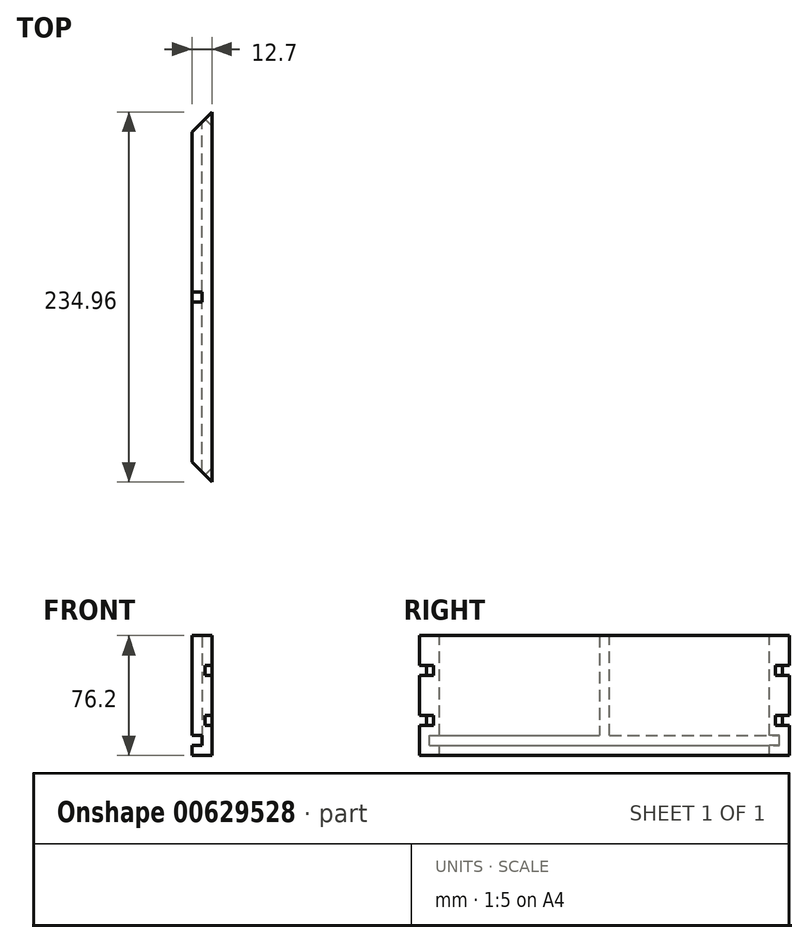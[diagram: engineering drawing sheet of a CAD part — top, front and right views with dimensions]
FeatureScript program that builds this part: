
annotation { "Feature Type Name" : "Feature", "Feature Type Description" : "" }
export const myFeature = defineFeature(function(context is Context, id is Id, definition is map)
    precondition{}
    {
        {
            var Q0;
            Q0=qCreatedBy(makeId("Right.planeOp"),FACE);
            var sketch = newSketch(context, id + "F0", { "sketchPlane" : qUnion([Q0])});
            skLineSegment(sketch, "E0.bottom", {"start": v(-117.47, 0) * mm, "end": v(117.48, 0) * mm});
            skLineSegment(sketch, "E0.top", {"start": v(-117.47, 76.2) * mm, "end": v(117.47, 76.2) * mm});
            skLineSegment(sketch, "E0.left", {"start": v(-117.47, 0) * mm, "end": v(-117.48, 76.2) * mm});
            skLineSegment(sketch, "E0.right", {"start": v(117.48, 0) * mm, "end": v(117.47, 76.2) * mm});
            skSolve(sketch);
        }
        {
            var Q0;
            Q0=makeQuery(id+"F0.imprint","IMPRINT",FACE,{"disambiguationData":[TD([[makeQuery(id+"F0.imprint","IMPRINT",EDGE,{"derivedFrom":sQuery(id+"F0.wireOp",EDGE,"E0.bottom")}),1.0]])]});
            extrude(context, id + "F1", {"entities" : qUnion([Q0]), "depth" : 12.7 * mm, "offsetDistance" : 25.4 * mm});
        }
        {
            var Q0;
            Q0=makeQuery(id+"F1.opExtrude","SWEPT_FACE",FACE,{"disambiguationData":[OSD([sQuery(id+"F0.wireOp",EDGE,"E0.right")])]});
            var sketch = newSketch(context, id + "F2", { "sketchPlane" : qUnion([Q0])});
            skLineSegment(sketch, "E1.bottom", {"start": v(0, 12.7) * mm, "end": v(-6.35, 12.7) * mm});
            skLineSegment(sketch, "E1.top", {"start": v(0, 6.35) * mm, "end": v(-6.35, 6.35) * mm});
            skLineSegment(sketch, "E1.left", {"start": v(0, 12.7) * mm, "end": v(0, 6.35) * mm});
            skLineSegment(sketch, "E1.right", {"start": v(-6.35, 12.7) * mm, "end": v(-6.35, 6.35) * mm});
            skSolve(sketch);
        }
        {
            var Q0;
            Q0 = qSketchRegion(id + "F2", true);
            extrude(context, id + "F3", {"entities" : qUnion([Q0]), "operationType" : NewBodyOperationType.REMOVE, "endBound" : BoundingType.THROUGH_ALL, "oppositeDirection" : true, "depth" : 25.4 * mm, "offsetDistance" : 25.4 * mm});
        }
        {
            var Q0;
            Q0=makeQuery(id+"F1.opExtrude","SWEPT_FACE",FACE,{"disambiguationData":[OSD([sQuery(id+"F0.wireOp",EDGE,"E0.top")])]});
            var sketch = newSketch(context, id + "F4", { "sketchPlane" : qUnion([Q0])});
            skLineSegment(sketch, "E2", {"start": v(12.7, 117.47) * mm, "end": v(0, 104.77) * mm});
            skLineSegment(sketch, "E3", {"start": v(0, 104.77) * mm, "end": v(0, 117.47) * mm});
            skLineSegment(sketch, "E4", {"start": v(0, 117.47) * mm, "end": v(12.7, 117.47) * mm});
            skLineSegment(sketch, "E5.MirrorCS", {"start": v(0, -117.47) * mm, "end": v(12.7, -117.47) * mm});
            skLineSegment(sketch, "E6.MirrorCS", {"start": v(12.7, -117.47) * mm, "end": v(0, -104.77) * mm});
            skLineSegment(sketch, "E7.MirrorCS", {"start": v(0, -104.77) * mm, "end": v(0, -117.47) * mm});
            skSolve(sketch);
        }
        {
            var Q0;
            Q0 = qSketchRegion(id + "F4", true);
            extrude(context, id + "F5", {"entities" : qUnion([Q0]), "operationType" : NewBodyOperationType.REMOVE, "endBound" : BoundingType.THROUGH_ALL, "oppositeDirection" : true, "depth" : 25.4 * mm, "offsetDistance" : 25.4 * mm});
        }
        {
            var Q0;
            {var subQ0=sQuery(id+"F0.wireOp",EDGE,"E0.top");var subQ1=sQuery(id+"F0.wireOp",EDGE,"E0.left");var subQ2=sQuery(id+"F0.wireOp",EDGE,"E0.right");Q0=makeQuery(id+"F3.boolean.opBoolean","SPLIT",FACE,{"disambiguationData":[TD([makeQuery(id+"F1.opExtrude","SWEPT_FACE",FACE,{"disambiguationData":[OSD([subQ0])]})])],"derivedFrom":makeQuery(id+"F1.opExtrude","CAP_FACE",FACE,{"disambiguationData":[OSD([sQuery(id+"F0.wireOp",EDGE,"E0.bottom"),subQ0,subQ1,subQ2])],"isStart":true})});}
            var sketch = newSketch(context, id + "F6", { "sketchPlane" : qUnion([Q0])});
            skLineSegment(sketch, "E8", {"start": v(-3.17, 12.7) * mm, "end": v(-3.18, 76.2) * mm});
            skLineSegment(sketch, "E9", {"start": v(3.17, 76.2) * mm, "end": v(3.18, 12.7) * mm});
            skLineSegment(sketch, "E10", {"start": v(-3.18, 76.2) * mm, "end": v(3.17, 76.2) * mm});
            skLineSegment(sketch, "E11", {"start": v(-3.17, 12.7) * mm, "end": v(3.18, 12.7) * mm});
            skSolve(sketch);
        }
        {
            var Q0;
            Q0 = qSketchRegion(id + "F6", true);
            extrude(context, id + "F7", {"entities" : qUnion([Q0]), "operationType" : NewBodyOperationType.REMOVE, "oppositeDirection" : true, "depth" : 6.35 * mm, "offsetDistance" : 25.4 * mm});
        }
        {
            var Q0;
            Q0=makeQuery(id+"F5.boolean.opBoolean","COPY",FACE,{"derivedFrom":makeQuery(id+"F5.opExtrude","SWEPT_FACE",FACE,{"disambiguationData":[OSD([sQuery(id+"F4.wireOp",EDGE,"E6.MirrorCS")])]})});
            var sketch = newSketch(context, id + "F8", { "sketchPlane" : qUnion([Q0])});
            skLineSegment(sketch, "E12.bottom", {"start": v(92.05, 57.15) * mm, "end": v(85.7, 57.15) * mm});
            skLineSegment(sketch, "E12.top", {"start": v(92.05, 50.8) * mm, "end": v(85.7, 50.8) * mm});
            skLineSegment(sketch, "E12.left", {"start": v(92.05, 57.15) * mm, "end": v(92.05, 50.8) * mm});
            skLineSegment(sketch, "E12.right", {"start": v(85.7, 57.15) * mm, "end": v(85.7, 50.8) * mm});
            skLineSegment(sketch, "E13.bottom", {"start": v(92.05, 25.4) * mm, "end": v(85.7, 25.4) * mm});
            skLineSegment(sketch, "E13.top", {"start": v(92.05, 19.05) * mm, "end": v(85.7, 19.05) * mm});
            skLineSegment(sketch, "E13.left", {"start": v(92.05, 25.4) * mm, "end": v(92.05, 19.05) * mm});
            skLineSegment(sketch, "E13.right", {"start": v(85.7, 25.4) * mm, "end": v(85.7, 19.05) * mm});
            skSolve(sketch);
        }
        {
            var Q0;
            Q0 = qSketchRegion(id + "F8", true);
            extrude(context, id + "F9", {"entities" : qUnion([Q0]), "operationType" : NewBodyOperationType.REMOVE, "endBound" : BoundingType.THROUGH_ALL, "oppositeDirection" : true, "depth" : 25.4 * mm, "offsetDistance" : 25.4 * mm});
        }
        {
            var Q0;
            Q0=makeQuery(id+"F5.boolean.opBoolean","COPY",FACE,{"derivedFrom":makeQuery(id+"F5.opExtrude","SWEPT_FACE",FACE,{"disambiguationData":[OSD([sQuery(id+"F4.wireOp",EDGE,"E2")])]})});
            var sketch = newSketch(context, id + "F10", { "sketchPlane" : qUnion([Q0])});
            skLineSegment(sketch, "E14.bottom", {"start": v(-92.05, 57.15) * mm, "end": v(-85.7, 57.15) * mm});
            skLineSegment(sketch, "E14.top", {"start": v(-92.05, 50.8) * mm, "end": v(-85.7, 50.8) * mm});
            skLineSegment(sketch, "E14.left", {"start": v(-92.05, 57.15) * mm, "end": v(-92.05, 50.8) * mm});
            skLineSegment(sketch, "E14.right", {"start": v(-85.7, 57.15) * mm, "end": v(-85.7, 50.8) * mm});
            skLineSegment(sketch, "E15.bottom", {"start": v(-92.05, 25.4) * mm, "end": v(-85.7, 25.4) * mm});
            skLineSegment(sketch, "E15.top", {"start": v(-92.05, 19.05) * mm, "end": v(-85.7, 19.05) * mm});
            skLineSegment(sketch, "E15.left", {"start": v(-92.05, 25.4) * mm, "end": v(-92.05, 19.05) * mm});
            skLineSegment(sketch, "E15.right", {"start": v(-85.7, 25.4) * mm, "end": v(-85.7, 19.05) * mm});
            skSolve(sketch);
        }
        {
            var Q0;
            Q0 = qSketchRegion(id + "F10", true);
            extrude(context, id + "F11", {"entities" : qUnion([Q0]), "operationType" : NewBodyOperationType.REMOVE, "endBound" : BoundingType.THROUGH_ALL, "oppositeDirection" : true, "depth" : 25.4 * mm, "offsetDistance" : 25.4 * mm});
        }
    });
